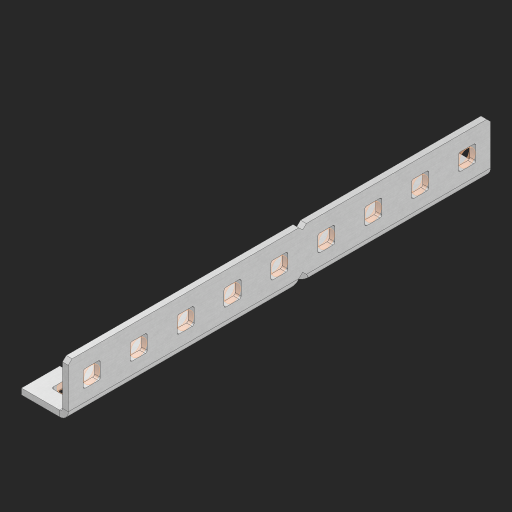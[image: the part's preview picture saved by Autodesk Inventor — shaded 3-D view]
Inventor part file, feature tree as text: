
AUTODESK INVENTOR PART (.ipt)
format: ipt  version: 2023 (Build 270158000, 158)  size: 690,176 bytes
history: native  units: in
note: dims shown in document units (in); Inventor stores cm internally (conversion verified against a paired STEP export)
features: other x175, extrude x25, sheet_metal_op x11, sketch x10, pattern_linear x2, mirror x1, chamfer x1
ambient origin geometry x8: Origin, YZ Plane, XZ Plane, XY Plane, X Axis, Y Axis, Z Axis, Center Point
bodies: Solid1 (feature_tree), Body (feature_tree)
feature tree (225):
  other  "Alu Half C 1x2x1x9"
  other  "Table"
  other  "Alu C 1x2x1x35"
  other  "Alu C 1x2x1x34"
  other  "Alu C 1x2x1x33"
  other  "Alu C 1x2x1x32"
  other  "Alu C 1x2x1x31"
  other  "Alu C 1x2x1x30"
  other  "Alu C 1x2x1x29"
  other  "Alu C 1x2x1x28"
  other  "Alu C 1x2x1x27"
  other  "Alu C 1x2x1x26"
  other  "Alu C 1x2x1x25"
  other  "Alu C 1x2x1x24"
  other  "Alu C 1x2x1x23"
  other  "Alu C 1x2x1x22"
  other  "Alu C 1x2x1x21"
  other  "Alu C 1x2x1x20"
  other  "Alu C 1x2x1x19"
  other  "Alu C 1x2x1x18"
  other  "Alu C 1x2x1x17"
  other  "Alu C 1x2x1x16"
  other  "Alu C 1x2x1x15"
  other  "Alu C 1x2x1x14"
  other  "Alu C 1x2x1x13"
  other  "Alu C 1x2x1x12"
  other  "Alu C 1x2x1x11"
  other  "Alu C 1x2x1x10"
  other  "Alu C 1x2x1x9"
  other  "Alu C 1x2x1x8"
  other  "Alu C 1x2x1x7"
  other  "Alu C 1x2x1x6"
  other  "Alu C 1x2x1x5"
  other  "Alu C 1x2x1x4"
  other  "Alu C 1x2x1x3"
  other  "Alu C 1x2x1x2"
  other  "Alu C 1x2x1x1"
  other  "Steel C 1x2x1x35"
  other  "Steel C 1x2x1x34"
  other  "Steel C 1x2x1x33"
  other  "Steel C 1x2x1x32"
  other  "Steel C 1x2x1x31"
  other  "Steel C 1x2x1x30"
  other  "Steel C 1x2x1x29"
  other  "Steel C 1x2x1x28"
  other  "Steel C 1x2x1x27"
  other  "Steel C 1x2x1x26"
  other  "Steel C 1x2x1x25"
  other  "Steel C 1x2x1x24"
  other  "Steel C 1x2x1x23"
  other  "Steel C 1x2x1x22"
  other  "Steel C 1x2x1x21"
  other  "Steel C 1x2x1x20"
  other  "Steel C 1x2x1x19"
  other  "Steel C 1x2x1x18"
  other  "Steel C 1x2x1x17"
  other  "Steel C 1x2x1x16"
  other  "Steel C 1x2x1x15"
  other  "Steel C 1x2x1x14"
  other  "Steel C 1x2x1x13"
  other  "Steel C 1x2x1x12"
  other  "Steel C 1x2x1x11"
  other  "Steel C 1x2x1x10"
  other  "Steel C 1x2x1x9"
  other  "Steel C 1x2x1x8"
  other  "Steel C 1x2x1x7"
  other  "Steel C 1x2x1x6"
  other  "Steel C 1x2x1x5"
  other  "Steel C 1x2x1x4"
  other  "Steel C 1x2x1x3"
  other  "Steel C 1x2x1x2"
  other  "Steel C 1x2x1x1"
  other  "Alu Half C 1x2x1x35"
  other  "Alu Half C 1x2x1x34"
  other  "Alu Half C 1x2x1x33"
  other  "Alu Half C 1x2x1x32"
  other  "Alu Half C 1x2x1x31"
  other  "Alu Half C 1x2x1x30"
  other  "Alu Half C 1x2x1x29"
  other  "Alu Half C 1x2x1x28"
  other  "Alu Half C 1x2x1x27"
  other  "Alu Half C 1x2x1x26"
  other  "Alu Half C 1x2x1x25"
  other  "Alu Half C 1x2x1x24"
  other  "Alu Half C 1x2x1x23"
  other  "Alu Half C 1x2x1x22"
  other  "Alu Half C 1x2x1x21"
  other  "Alu Half C 1x2x1x20"
  other  "Alu Half C 1x2x1x19"
  other  "Alu Half C 1x2x1x18"
  other  "Alu Half C 1x2x1x17"
  other  "Alu Half C 1x2x1x16"
  other  "Alu Half C 1x2x1x15"
  other  "Alu Half C 1x2x1x14"
  other  "Alu Half C 1x2x1x13"
  other  "Alu Half C 1x2x1x12"
  other  "Alu Half C 1x2x1x11"
  other  "Alu Half C 1x2x1x10"
  other  "Alu Half C 1x2x1x8"
  other  "Alu Half C 1x2x1x7"
  other  "Alu Half C 1x2x1x6"
  other  "Alu Half C 1x2x1x5"
  other  "Alu Half C 1x2x1x4"
  other  "Alu Half C 1x2x1x3"
  other  "Alu Half C 1x2x1x2"
  other  "Alu Half C 1x2x1x1"
  other  "Steel Half C 1x2x1x35"
  other  "Steel Half C 1x2x1x34"
  other  "Steel Half C 1x2x1x33"
  other  "Steel Half C 1x2x1x32"
  other  "Steel Half C 1x2x1x31"
  other  "Steel Half C 1x2x1x30"
  other  "Steel Half C 1x2x1x29"
  other  "Steel Half C 1x2x1x28"
  other  "Steel Half C 1x2x1x27"
  other  "Steel Half C 1x2x1x26"
  other  "Steel Half C 1x2x1x25"
  other  "Steel Half C 1x2x1x24"
  other  "Steel Half C 1x2x1x23"
  other  "Steel Half C 1x2x1x22"
  other  "Steel Half C 1x2x1x21"
  other  "Steel Half C 1x2x1x20"
  other  "Steel Half C 1x2x1x19"
  other  "Steel Half C 1x2x1x18"
  other  "Steel Half C 1x2x1x17"
  other  "Steel Half C 1x2x1x16"
  other  "Steel Half C 1x2x1x15"
  other  "Steel Half C 1x2x1x14"
  other  "Steel Half C 1x2x1x13"
  other  "Steel Half C 1x2x1x12"
  other  "Steel Half C 1x2x1x11"
  other  "Steel Half C 1x2x1x10"
  other  "Steel Half C 1x2x1x9"
  other  "Steel Half C 1x2x1x8"
  other  "Steel Half C 1x2x1x7"
  other  "Steel Half C 1x2x1x6"
  other  "Steel Half C 1x2x1x5"
  other  "Steel Half C 1x2x1x4"
  other  "Steel Half C 1x2x1x3"
  other  "Steel Half C 1x2x1x2"
  other  "Steel Half C 1x2x1x1"
  sheet_metal_op  "Flanges"
  other  "Flange Pattern Plane"
  other  "Flange Pattern Sketch"
  sheet_metal_op  "Flange Pattern"
  sheet_metal_op  "Body Pattern"
  pattern_linear  "Center Pattern"  Spacing1=0.0625in  [1 undecoded]
  other  "Arc Length"
  mirror  "Notch Mirror"
  pattern_linear  "Notch Pattern"  Spacing1=0.182in  [1 undecoded]
  chamfer  "End Chamfer"
  extrude  "Half Cut"  Depth=0.02in
  sketch  "Sketch1"  dims[d0=1.0in]
  other  "Plate1"
  sketch  "Sketch2"  dims[d1=4.5in]
  other  "Plate2"
  sheet_metal_op  "Bend1"
  sheet_metal_op  "Corner1"
  sketch  "Sketch3"  dims[d2=0.0625in]
  sketch  "Sketch7"  dims[d3=0.0625in]
  other  "Srf1"
  other  "Srf2"
  sketch  "Sketch8"  dims[d4=0.0312in]
  sketch  "Sketch9"  dims[d5=0.125in]
  other  "Srf91"
  sheet_metal_op  "Body Pattern Sketch"
  other  "Srf92"
  sketch  "Sketch13"  dims[d6=0.0625in]
  sketch  "Sketch14"  dims[d7=0.5in d8=90.0deg d9=0.0312in]
  sketch  "Sketch15"  dims[d10=0.25in]
  sketch  "Sketch16"  dims[d11=0.0625in d12=0.0625in d16=0.182in d17=0.02in d18=0.0625in d19=0.0in d20=0.25in d21=0.25in d38=3.5433in d40=0.5in d41=0.3937in d43=1.0in d46=0.172in d47=1.0in d48=0.0in d49=0.182in d50=0.02in d51=0.25in d52=0.25in d53=0.0625in d54=0.0in d55=0.172in d56=1.0in d57=0.0in d58=0.25in d60=3.5433in d62=0.5in d63=0.3937in d65=0.5in d85=0.1473in d86=0.1782in d88=0.04in d89=0.0625in d90=0.0in d91=0.04in d92=0.0491in d95=2.5in d96=0.04in d97=0.25in d98=45.0deg d99=0.25in d100=0.5in d101=0.0in d102=2.497in d106=0.182in d107=0.02in d108=0.5in d109=0.5in d110=0.0625in d111=0.0in d112=0.172in d113=0.5in d114=0.0in d117=0.5in d118=0.5in d119=0.5in]
  other  "Srf786"
  other  "Srf823"
  other  "Srf824"
  other  "Srf825"
  other  "Srf826"
  other  "Srf827"
  other  "Srf828"
  other  "Srf829"
  other  "Srf856"
  other  "Srf857"
  other  "Srf858"
  other  "Srf859"
  other  "Srf860"
  other  "Srf861"
  other  "Srf862"
  other  "Srf889"
  other  "Srf890"
  other  "Srf891"
  other  "Srf892"
  other  "Srf893"
  other  "Srf894"
  other  "Srf895"
  other  "Srf896"
  sheet_metal_op  "Flange Stamp"
  sheet_metal_op  "Flange Circle"
  sheet_metal_op  "Body Stamp"
  sheet_metal_op  "Body Circle"
  other  "Center Stamp"
  other  "Center Circle"
  sheet_metal_op  "Notch"
  extrude  "ExtrusionSrf2"  Depth=0.0625in
  extrude  "ExtrusionSrf92"  TaperAngle=0.0deg  [1 undecoded]
  extrude  "ExtrusionSrf823"  Depth=0.5in
  extrude  "ExtrusionSrf824"  Depth=0.5in
  extrude  "ExtrusionSrf825"  Depth=0.5in
  extrude  "ExtrusionSrf826"  Depth=0.5in
  extrude  "ExtrusionSrf827"  Depth=1.0in TaperAngle=0.0deg
  extrude  "ExtrusionSrf828"  Depth=0.182in
  extrude  "ExtrusionSrf829"  Depth=0.02in
  extrude  "ExtrusionSrf856"  Depth=0.5in
  extrude  "ExtrusionSrf857"  Depth=0.5in
  extrude  "ExtrusionSrf858"  Depth=0.0625in
  extrude  "ExtrusionSrf859"  TaperAngle=0.0deg  [1 undecoded]
  extrude  "ExtrusionSrf860"  Depth=0.5in
  extrude  "ExtrusionSrf861"  Depth=1.0in TaperAngle=0.0deg
  extrude  "ExtrusionSrf862"  Depth=0.5in
  extrude  "ExtrusionSrf889"  Depth=0.5in
  extrude  "ExtrusionSrf890"  Depth=0.5in
  extrude  "ExtrusionSrf891"  Depth=0.5in
  extrude  "ExtrusionSrf892"  Depth=0.5in
  extrude  "ExtrusionSrf893"  Depth=0.5in
  extrude  "ExtrusionSrf894"  Depth=0.0625in
  extrude  "ExtrusionSrf895"  TaperAngle=0.0deg  [1 undecoded]
  extrude  "ExtrusionSrf896"  Depth=0.5in
note: 5 required parameter values undecoded (feature->parameter linkage not recoverable at this tier; creation-order binding heuristic only, values carry confidence <= 0.55)
